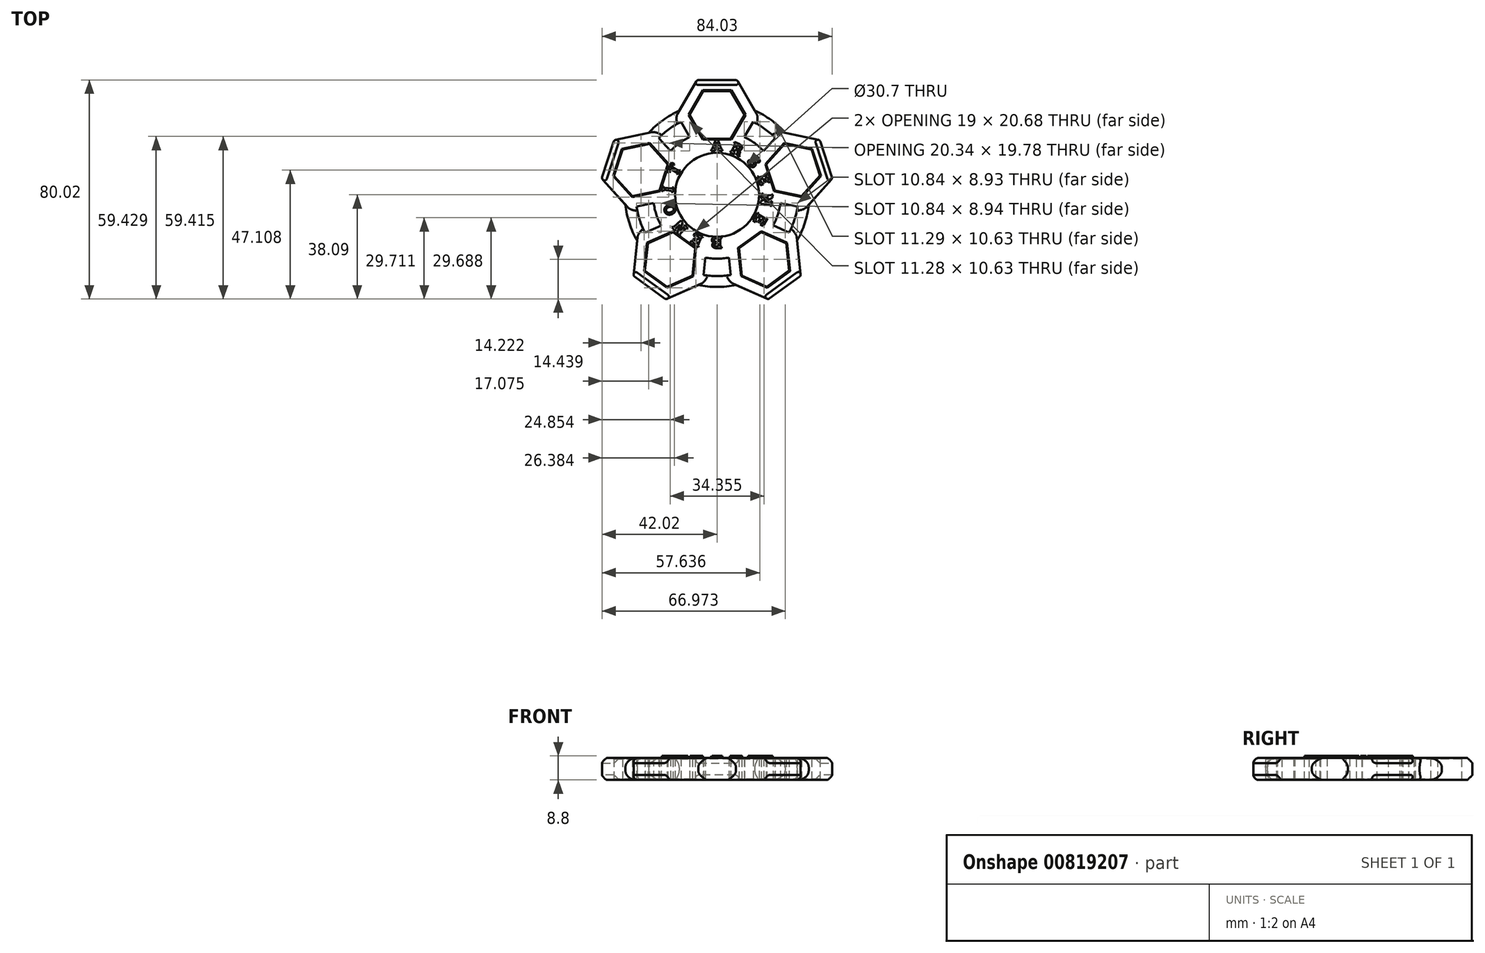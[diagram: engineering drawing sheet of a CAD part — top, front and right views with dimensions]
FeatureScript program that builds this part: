
annotation { "Feature Type Name" : "Feature", "Feature Type Description" : "" }
export const myFeature = defineFeature(function(context is Context, id is Id, definition is map)
    precondition{}
    {
        {
            var Q0;
            Q0=qCreatedBy(makeId("Top.planeOp"),FACE);
            var sketch = newSketch(context, id + "F0", { "sketchPlane" : qUnion([Q0])});
            skCircle(sketch, "E0", {"center": v(0, 0) * mm, "radius": 15.35 * mm});
            skCircle(sketch, "E1", {"center": v(0, 0) * mm, "radius": 23.35 * mm});
            skCircle(sketch, "E2.cCircle", {"center": v(-0.01, 29.22) * mm, "radius": 10.05 * mm, "construction": true});
            skLineSegment(sketch, "E2.0", {"start": v(-5.04, 20.52) * mm, "end": v(-10.06, 29.22) * mm});
            skLineSegment(sketch, "E2.1", {"start": v(-10.06, 29.22) * mm, "end": v(-5.04, 37.93) * mm});
            skLineSegment(sketch, "E2.2", {"start": v(-5.04, 37.93) * mm, "end": v(5.01, 37.93) * mm});
            skLineSegment(sketch, "E2.3", {"start": v(5.01, 37.93) * mm, "end": v(10.04, 29.22) * mm});
            skLineSegment(sketch, "E2.4", {"start": v(10.04, 29.22) * mm, "end": v(5.01, 20.52) * mm});
            skLineSegment(sketch, "E2.5", {"start": v(5.01, 20.52) * mm, "end": v(-5.04, 20.52) * mm});
            skCircle(sketch, "E3", {"center": v(0, 0) * mm, "radius": 29.73 * mm});
            skCircle(sketch, "E4", {"center": v(0, 0) * mm, "radius": 39.45 * mm});
            skLineSegment(sketch, "E5.0", {"start": v(-14.68, 29.22) * mm, "end": v(-7.35, 41.93) * mm});
            skLineSegment(sketch, "E5.1", {"start": v(7.32, 41.93) * mm, "end": v(14.65, 29.22) * mm});
            skLineSegment(sketch, "E5.2", {"start": v(14.65, 29.22) * mm, "end": v(7.32, 16.52) * mm});
            skLineSegment(sketch, "E5.3", {"start": v(-7.35, 41.93) * mm, "end": v(7.32, 41.93) * mm});
            skLineSegment(sketch, "E5.4", {"start": v(7.32, 16.52) * mm, "end": v(-7.35, 16.52) * mm});
            skLineSegment(sketch, "E5.5", {"start": v(-7.35, 16.52) * mm, "end": v(-14.68, 29.22) * mm});
            skCircle(sketch, "E6", {"center": v(0, 0) * mm, "radius": 33.7 * mm});
            skLineSegment(sketch, "E7.1.0", {"start": v(-42.15, 5.97) * mm, "end": v(-37.61, 19.92) * mm});
            skCircle(sketch, "E7.1.1", {"center": v(-27.8, 9.02) * mm, "radius": 10.05 * mm, "construction": true});
            skLineSegment(sketch, "E7.1.2", {"start": v(-37.63, 6.93) * mm, "end": v(-34.52, 16.49) * mm});
            skLineSegment(sketch, "E7.1.3", {"start": v(-34.52, 16.49) * mm, "end": v(-24.7, 18.58) * mm});
            skLineSegment(sketch, "E7.1.4", {"start": v(-30.9, -0.54) * mm, "end": v(-37.63, 6.93) * mm});
            skLineSegment(sketch, "E7.1.5", {"start": v(-21.07, 1.55) * mm, "end": v(-30.9, -0.54) * mm});
            skLineSegment(sketch, "E7.1.6", {"start": v(-17.97, 11.1) * mm, "end": v(-21.07, 1.55) * mm});
            skLineSegment(sketch, "E7.1.7", {"start": v(-24.7, 18.58) * mm, "end": v(-17.97, 11.1) * mm});
            skLineSegment(sketch, "E7.1.8", {"start": v(-37.61, 19.92) * mm, "end": v(-23.27, 22.97) * mm});
            skLineSegment(sketch, "E7.1.9", {"start": v(-17.98, -1.88) * mm, "end": v(-32.33, -4.93) * mm});
            skLineSegment(sketch, "E7.1.10", {"start": v(-13.45, 12.07) * mm, "end": v(-17.98, -1.88) * mm});
            skLineSegment(sketch, "E7.1.11", {"start": v(-23.27, 22.97) * mm, "end": v(-13.45, 12.07) * mm});
            skLineSegment(sketch, "E7.1.12", {"start": v(-32.33, -4.93) * mm, "end": v(-42.15, 5.97) * mm});
            skLineSegment(sketch, "E7.2.0", {"start": v(-18.7, -38.24) * mm, "end": v(-30.57, -29.62) * mm});
            skCircle(sketch, "E7.2.1", {"center": v(-17.17, -23.65) * mm, "radius": 10.05 * mm, "construction": true});
            skLineSegment(sketch, "E7.2.2", {"start": v(-18.22, -33.65) * mm, "end": v(-26.35, -27.74) * mm});
            skLineSegment(sketch, "E7.2.3", {"start": v(-26.35, -27.74) * mm, "end": v(-25.3, -17.74) * mm});
            skLineSegment(sketch, "E7.2.4", {"start": v(-9.04, -29.56) * mm, "end": v(-18.22, -33.65) * mm});
            skLineSegment(sketch, "E7.2.5", {"start": v(-7.99, -19.56) * mm, "end": v(-9.04, -29.56) * mm});
            skLineSegment(sketch, "E7.2.6", {"start": v(-16.12, -13.66) * mm, "end": v(-7.99, -19.56) * mm});
            skLineSegment(sketch, "E7.2.7", {"start": v(-25.3, -17.74) * mm, "end": v(-16.12, -13.66) * mm});
            skLineSegment(sketch, "E7.2.8", {"start": v(-30.57, -29.62) * mm, "end": v(-29.03, -15.03) * mm});
            skLineSegment(sketch, "E7.2.9", {"start": v(-3.77, -17.68) * mm, "end": v(-5.3, -32.27) * mm});
            skLineSegment(sketch, "E7.2.10", {"start": v(-15.63, -9.06) * mm, "end": v(-3.77, -17.68) * mm});
            skLineSegment(sketch, "E7.2.11", {"start": v(-29.03, -15.03) * mm, "end": v(-15.63, -9.06) * mm});
            skLineSegment(sketch, "E7.2.12", {"start": v(-5.3, -32.27) * mm, "end": v(-18.7, -38.24) * mm});
            skLineSegment(sketch, "E7.3.0", {"start": v(30.59, -29.6) * mm, "end": v(18.72, -38.22) * mm});
            skCircle(sketch, "E7.3.1", {"center": v(17.19, -23.63) * mm, "radius": 10.05 * mm, "construction": true});
            skLineSegment(sketch, "E7.3.2", {"start": v(26.37, -27.72) * mm, "end": v(18.24, -33.63) * mm});
            skLineSegment(sketch, "E7.3.3", {"start": v(18.24, -33.63) * mm, "end": v(9.06, -29.54) * mm});
            skLineSegment(sketch, "E7.3.4", {"start": v(25.32, -17.73) * mm, "end": v(26.37, -27.72) * mm});
            skLineSegment(sketch, "E7.3.5", {"start": v(16.14, -13.64) * mm, "end": v(25.32, -17.73) * mm});
            skLineSegment(sketch, "E7.3.6", {"start": v(8, -19.55) * mm, "end": v(16.14, -13.64) * mm});
            skLineSegment(sketch, "E7.3.7", {"start": v(9.06, -29.54) * mm, "end": v(8, -19.55) * mm});
            skLineSegment(sketch, "E7.3.8", {"start": v(18.72, -38.22) * mm, "end": v(5.32, -32.26) * mm});
            skLineSegment(sketch, "E7.3.9", {"start": v(15.66, -9.05) * mm, "end": v(29.06, -15.01) * mm});
            skLineSegment(sketch, "E7.3.10", {"start": v(3.79, -17.67) * mm, "end": v(15.66, -9.05) * mm});
            skLineSegment(sketch, "E7.3.11", {"start": v(5.32, -32.26) * mm, "end": v(3.79, -17.67) * mm});
            skLineSegment(sketch, "E7.3.12", {"start": v(29.06, -15.01) * mm, "end": v(30.59, -29.6) * mm});
            skLineSegment(sketch, "E7.4.0", {"start": v(37.6, 19.95) * mm, "end": v(42.14, 6) * mm});
            skCircle(sketch, "E7.4.1", {"center": v(27.79, 9.04) * mm, "radius": 10.05 * mm, "construction": true});
            skLineSegment(sketch, "E7.4.2", {"start": v(34.51, 16.51) * mm, "end": v(37.62, 6.95) * mm});
            skLineSegment(sketch, "E7.4.3", {"start": v(37.62, 6.95) * mm, "end": v(30.9, -0.51) * mm});
            skLineSegment(sketch, "E7.4.4", {"start": v(24.68, 18.6) * mm, "end": v(34.51, 16.51) * mm});
            skLineSegment(sketch, "E7.4.5", {"start": v(17.96, 11.13) * mm, "end": v(24.68, 18.6) * mm});
            skLineSegment(sketch, "E7.4.6", {"start": v(21.06, 1.58) * mm, "end": v(17.96, 11.13) * mm});
            skLineSegment(sketch, "E7.4.7", {"start": v(30.9, -0.51) * mm, "end": v(21.06, 1.58) * mm});
            skLineSegment(sketch, "E7.4.8", {"start": v(42.14, 6) * mm, "end": v(32.32, -4.9) * mm});
            skLineSegment(sketch, "E7.4.9", {"start": v(13.44, 12.1) * mm, "end": v(23.26, 23) * mm});
            skLineSegment(sketch, "E7.4.10", {"start": v(17.97, -1.86) * mm, "end": v(13.44, 12.1) * mm});
            skLineSegment(sketch, "E7.4.11", {"start": v(32.32, -4.9) * mm, "end": v(17.97, -1.86) * mm});
            skLineSegment(sketch, "E7.4.12", {"start": v(23.26, 23) * mm, "end": v(37.6, 19.95) * mm});
            skSolve(sketch);
        }
        {
            var Q0;
            {var subQ1=sQuery(id+"F0.wireOp",EDGE,"E2.0");var subQ5=sQuery(id+"F0.wireOp",EDGE,"E2.1");var subQ6=makeQuery(id+"F0.imprint","INTERSECT",VERTEX,{"derivedFrom":[subQ1,subQ5]});Q0=makeQuery(id+"F0.imprint","IMPRINT",FACE,{"disambiguationData":[TD([[makeQuery(id+"F0.imprint","IMPRINT",EDGE,{"disambiguationData":[TD([[subQ6,1.0]])],"derivedFrom":subQ1}),1.0]])]});}
            var Q1;
            {var subQ1=sQuery(id+"F0.wireOp",EDGE,"E2.4");var subQ9=sQuery(id+"F0.wireOp",EDGE,"E2.3");var subQ10=makeQuery(id+"F0.imprint","INTERSECT",VERTEX,{"derivedFrom":[subQ9,subQ1]});Q1=makeQuery(id+"F0.imprint","IMPRINT",FACE,{"disambiguationData":[TD([[makeQuery(id+"F0.imprint","IMPRINT",EDGE,{"disambiguationData":[TD([[subQ10,1.0]])],"derivedFrom":subQ9}),1.0]])]});}
            var Q2;
            {var subQ5=sQuery(id+"F0.wireOp",EDGE,"E3");var subQ9=sQuery(id+"F0.wireOp",EDGE,"E7.4.9");var subQ10=makeQuery(id+"F0.imprint","INTERSECT",VERTEX,{"derivedFrom":[subQ5,subQ9]});Q2=makeQuery(id+"F0.imprint","IMPRINT",FACE,{"disambiguationData":[TD([[makeQuery(id+"F0.imprint","IMPRINT",EDGE,{"disambiguationData":[TD([[subQ10,1.0]])],"derivedFrom":subQ5}),-1.0]])]});}
            var Q3;
            {var subQ7=sQuery(id+"F0.wireOp",EDGE,"E3");var subQ9=sQuery(id+"F0.wireOp",EDGE,"E7.4.9");var subQ10=makeQuery(id+"F0.imprint","INTERSECT",VERTEX,{"derivedFrom":[subQ7,subQ9]});Q3=makeQuery(id+"F0.imprint","IMPRINT",FACE,{"disambiguationData":[TD([[makeQuery(id+"F0.imprint","IMPRINT",EDGE,{"disambiguationData":[TD([[subQ10,-1.0]])],"derivedFrom":subQ7}),-1.0]])]});}
            var Q4;
            {var subQ0=sQuery(id+"F0.wireOp",EDGE,"E5.5");var subQ3=sQuery(id+"F0.wireOp",EDGE,"E3");var subQ4=makeQuery(id+"F0.imprint","INTERSECT",VERTEX,{"derivedFrom":[subQ3,subQ0]});Q4=makeQuery(id+"F0.imprint","IMPRINT",FACE,{"disambiguationData":[TD([[makeQuery(id+"F0.imprint","IMPRINT",EDGE,{"disambiguationData":[TD([[subQ4,-1.0]])],"derivedFrom":subQ3}),-1.0]])]});}
            var Q5;
            {var subQ3=sQuery(id+"F0.wireOp",EDGE,"E3");var subQ9=sQuery(id+"F0.wireOp",EDGE,"E7.1.11");var subQ11=makeQuery(id+"F0.imprint","INTERSECT",VERTEX,{"derivedFrom":[subQ3,subQ9]});Q5=makeQuery(id+"F0.imprint","IMPRINT",FACE,{"disambiguationData":[TD([[makeQuery(id+"F0.imprint","IMPRINT",EDGE,{"disambiguationData":[TD([[subQ11,-1.0]])],"derivedFrom":subQ3}),-1.0]])]});}
            var Q6;
            {var subQ0=sQuery(id+"F0.wireOp",EDGE,"E7.1.5");var subQ3=sQuery(id+"F0.wireOp",EDGE,"E3");var subQ4=makeQuery(id+"F0.imprint","INTERSECT",VERTEX,{"derivedFrom":[subQ3,subQ0]});Q6=makeQuery(id+"F0.imprint","IMPRINT",FACE,{"disambiguationData":[TD([[makeQuery(id+"F0.imprint","IMPRINT",EDGE,{"disambiguationData":[TD([[subQ4,-1.0]])],"derivedFrom":subQ3}),-1.0]])]});}
            var Q7;
            {var subQ1=sQuery(id+"F0.wireOp",EDGE,"E7.1.9");var subQ7=sQuery(id+"F0.wireOp",EDGE,"E3");var subQ8=makeQuery(id+"F0.imprint","INTERSECT",VERTEX,{"derivedFrom":[subQ7,subQ1]});Q7=makeQuery(id+"F0.imprint","IMPRINT",FACE,{"disambiguationData":[TD([[makeQuery(id+"F0.imprint","IMPRINT",EDGE,{"disambiguationData":[TD([[subQ8,-1.0]])],"derivedFrom":subQ7}),-1.0]])]});}
            var Q8;
            {var subQ5=sQuery(id+"F0.wireOp",EDGE,"E3");var subQ9=sQuery(id+"F0.wireOp",EDGE,"E7.2.11");var subQ11=makeQuery(id+"F0.imprint","INTERSECT",VERTEX,{"derivedFrom":[subQ5,subQ9]});Q8=makeQuery(id+"F0.imprint","IMPRINT",FACE,{"disambiguationData":[TD([[makeQuery(id+"F0.imprint","IMPRINT",EDGE,{"disambiguationData":[TD([[subQ11,-1.0]])],"derivedFrom":subQ5}),-1.0]])]});}
            var Q9;
            {var subQ0=sQuery(id+"F0.wireOp",EDGE,"E7.2.5");var subQ3=sQuery(id+"F0.wireOp",EDGE,"E3");var subQ4=makeQuery(id+"F0.imprint","INTERSECT",VERTEX,{"derivedFrom":[subQ3,subQ0]});Q9=makeQuery(id+"F0.imprint","IMPRINT",FACE,{"disambiguationData":[TD([[makeQuery(id+"F0.imprint","IMPRINT",EDGE,{"disambiguationData":[TD([[subQ4,-1.0]])],"derivedFrom":subQ3}),-1.0]])]});}
            var Q10;
            {var subQ1=sQuery(id+"F0.wireOp",EDGE,"E7.2.9");var subQ7=sQuery(id+"F0.wireOp",EDGE,"E3");var subQ8=makeQuery(id+"F0.imprint","INTERSECT",VERTEX,{"derivedFrom":[subQ7,subQ1]});Q10=makeQuery(id+"F0.imprint","IMPRINT",FACE,{"disambiguationData":[TD([[makeQuery(id+"F0.imprint","IMPRINT",EDGE,{"disambiguationData":[TD([[subQ8,-1.0]])],"derivedFrom":subQ7}),-1.0]])]});}
            var Q11;
            {var subQ3=sQuery(id+"F0.wireOp",EDGE,"E3");var subQ9=sQuery(id+"F0.wireOp",EDGE,"E7.3.11");var subQ11=makeQuery(id+"F0.imprint","INTERSECT",VERTEX,{"derivedFrom":[subQ3,subQ9]});Q11=makeQuery(id+"F0.imprint","IMPRINT",FACE,{"disambiguationData":[TD([[makeQuery(id+"F0.imprint","IMPRINT",EDGE,{"disambiguationData":[TD([[subQ11,-1.0]])],"derivedFrom":subQ3}),-1.0]])]});}
            var Q12;
            {var subQ0=sQuery(id+"F0.wireOp",EDGE,"E7.3.5");var subQ3=sQuery(id+"F0.wireOp",EDGE,"E3");var subQ4=makeQuery(id+"F0.imprint","INTERSECT",VERTEX,{"derivedFrom":[subQ3,subQ0]});Q12=makeQuery(id+"F0.imprint","IMPRINT",FACE,{"disambiguationData":[TD([[makeQuery(id+"F0.imprint","IMPRINT",EDGE,{"disambiguationData":[TD([[subQ4,-1.0]])],"derivedFrom":subQ3}),-1.0]])]});}
            var Q13;
            {var subQ1=sQuery(id+"F0.wireOp",EDGE,"E7.3.9");var subQ7=sQuery(id+"F0.wireOp",EDGE,"E3");var subQ8=makeQuery(id+"F0.imprint","INTERSECT",VERTEX,{"derivedFrom":[subQ7,subQ1]});Q13=makeQuery(id+"F0.imprint","IMPRINT",FACE,{"disambiguationData":[TD([[makeQuery(id+"F0.imprint","IMPRINT",EDGE,{"disambiguationData":[TD([[subQ8,-1.0]])],"derivedFrom":subQ7}),-1.0]])]});}
            var Q14;
            {var subQ3=sQuery(id+"F0.wireOp",EDGE,"E3");var subQ9=sQuery(id+"F0.wireOp",EDGE,"E7.4.11");var subQ11=makeQuery(id+"F0.imprint","INTERSECT",VERTEX,{"derivedFrom":[subQ3,subQ9]});Q14=makeQuery(id+"F0.imprint","IMPRINT",FACE,{"disambiguationData":[TD([[makeQuery(id+"F0.imprint","IMPRINT",EDGE,{"disambiguationData":[TD([[subQ11,-1.0]])],"derivedFrom":subQ3}),-1.0]])]});}
            var Q15;
            {var subQ5=sQuery(id+"F0.wireOp",EDGE,"E5.3");Q15=makeQuery(id+"F0.imprint","IMPRINT",FACE,{"disambiguationData":[TD([[makeQuery(id+"F0.imprint","IMPRINT",EDGE,{"derivedFrom":subQ5}),-1.0]])]});}
            var Q16;
            {var subQ1=sQuery(id+"F0.wireOp",EDGE,"E2.2");Q16=makeQuery(id+"F0.imprint","IMPRINT",FACE,{"disambiguationData":[TD([[makeQuery(id+"F0.imprint","IMPRINT",EDGE,{"derivedFrom":subQ1}),1.0]])]});}
            var Q17;
            {var subQ0=sQuery(id+"F0.wireOp",EDGE,"E7.4.2");Q17=makeQuery(id+"F0.imprint","IMPRINT",FACE,{"disambiguationData":[TD([[makeQuery(id+"F0.imprint","IMPRINT",EDGE,{"derivedFrom":subQ0}),1.0]])]});}
            var Q18;
            {var subQ0=sQuery(id+"F0.wireOp",EDGE,"E7.1.2");Q18=makeQuery(id+"F0.imprint","IMPRINT",FACE,{"disambiguationData":[TD([[makeQuery(id+"F0.imprint","IMPRINT",EDGE,{"derivedFrom":subQ0}),1.0]])]});}
            var Q19;
            {var subQ9=sQuery(id+"F0.wireOp",EDGE,"E7.2.2");Q19=makeQuery(id+"F0.imprint","IMPRINT",FACE,{"disambiguationData":[TD([[makeQuery(id+"F0.imprint","IMPRINT",EDGE,{"derivedFrom":subQ9}),1.0]])]});}
            var Q20;
            {var subQ0=sQuery(id+"F0.wireOp",EDGE,"E7.3.2");Q20=makeQuery(id+"F0.imprint","IMPRINT",FACE,{"disambiguationData":[TD([[makeQuery(id+"F0.imprint","IMPRINT",EDGE,{"derivedFrom":subQ0}),1.0]])]});}
            var Q21;
            {var subQ0=sQuery(id+"F0.wireOp",EDGE,"E5.2");var subQ1=sQuery(id+"F0.wireOp",EDGE,"E1");var subQ2=makeQuery(id+"F0.imprint","INTERSECT",VERTEX,{"derivedFrom":[subQ1,subQ0]});Q21=makeQuery(id+"F0.imprint","IMPRINT",FACE,{"disambiguationData":[TD([[makeQuery(id+"F0.imprint","IMPRINT",EDGE,{"disambiguationData":[TD([[subQ2,-1.0]])],"derivedFrom":subQ1}),-1.0]])]});}
            var Q22;
            {var subQ0=sQuery(id+"F0.wireOp",EDGE,"E2.0");var subQ1=sQuery(id+"F0.wireOp",EDGE,"E1");var subQ2=makeQuery(id+"F0.imprint","INTERSECT",VERTEX,{"derivedFrom":[subQ1,subQ0]});Q22=makeQuery(id+"F0.imprint","IMPRINT",FACE,{"disambiguationData":[TD([[makeQuery(id+"F0.imprint","IMPRINT",EDGE,{"disambiguationData":[TD([[subQ2,-1.0]])],"derivedFrom":subQ1}),-1.0]])]});}
            var Q23;
            {var subQ0=sQuery(id+"F0.wireOp",EDGE,"E2.5");Q23=makeQuery(id+"F0.imprint","IMPRINT",FACE,{"disambiguationData":[TD([[makeQuery(id+"F0.imprint","IMPRINT",EDGE,{"derivedFrom":subQ0}),1.0]])]});}
            var Q24;
            {var subQ5=sQuery(id+"F0.wireOp",EDGE,"E7.1.0");Q24=makeQuery(id+"F0.imprint","IMPRINT",FACE,{"disambiguationData":[TD([[makeQuery(id+"F0.imprint","IMPRINT",EDGE,{"derivedFrom":subQ5}),-1.0]])]});}
            var Q25;
            {var subQ0=sQuery(id+"F0.wireOp",EDGE,"E7.4.5");var subQ1=sQuery(id+"F0.wireOp",EDGE,"E1");var subQ2=makeQuery(id+"F0.imprint","INTERSECT",VERTEX,{"derivedFrom":[subQ1,subQ0]});Q25=makeQuery(id+"F0.imprint","IMPRINT",FACE,{"disambiguationData":[TD([[makeQuery(id+"F0.imprint","IMPRINT",EDGE,{"disambiguationData":[TD([[subQ2,-1.0]])],"derivedFrom":subQ1}),-1.0]])]});}
            var Q26;
            {var subQ0=sQuery(id+"F0.wireOp",EDGE,"E7.4.6");Q26=makeQuery(id+"F0.imprint","IMPRINT",FACE,{"disambiguationData":[TD([[makeQuery(id+"F0.imprint","IMPRINT",EDGE,{"derivedFrom":subQ0}),1.0]])]});}
            var Q27;
            Q27=makeQuery(id+"F0.imprint","IMPRINT",FACE,{"disambiguationData":[TD([[makeQuery(id+"F0.imprint","IMPRINT",EDGE,{"derivedFrom":sQuery(id+"F0.wireOp",EDGE,"E0")}),-1.0]])]});
            var Q28;
            {var subQ5=sQuery(id+"F0.wireOp",EDGE,"E7.4.0");Q28=makeQuery(id+"F0.imprint","IMPRINT",FACE,{"disambiguationData":[TD([[makeQuery(id+"F0.imprint","IMPRINT",EDGE,{"derivedFrom":subQ5}),-1.0]])]});}
            var Q29;
            {var subQ0=sQuery(id+"F0.wireOp",EDGE,"E7.1.6");Q29=makeQuery(id+"F0.imprint","IMPRINT",FACE,{"disambiguationData":[TD([[makeQuery(id+"F0.imprint","IMPRINT",EDGE,{"derivedFrom":subQ0}),1.0]])]});}
            var Q30;
            {var subQ0=sQuery(id+"F0.wireOp",EDGE,"E7.2.6");Q30=makeQuery(id+"F0.imprint","IMPRINT",FACE,{"disambiguationData":[TD([[makeQuery(id+"F0.imprint","IMPRINT",EDGE,{"derivedFrom":subQ0}),1.0]])]});}
            var Q31;
            {var subQ0=sQuery(id+"F0.wireOp",EDGE,"E7.3.6");Q31=makeQuery(id+"F0.imprint","IMPRINT",FACE,{"disambiguationData":[TD([[makeQuery(id+"F0.imprint","IMPRINT",EDGE,{"derivedFrom":subQ0}),1.0]])]});}
            var Q32;
            {var subQ0=sQuery(id+"F0.wireOp",EDGE,"E7.3.5");var subQ1=sQuery(id+"F0.wireOp",EDGE,"E1");var subQ2=makeQuery(id+"F0.imprint","INTERSECT",VERTEX,{"derivedFrom":[subQ1,subQ0]});Q32=makeQuery(id+"F0.imprint","IMPRINT",FACE,{"disambiguationData":[TD([[makeQuery(id+"F0.imprint","IMPRINT",EDGE,{"disambiguationData":[TD([[subQ2,-1.0]])],"derivedFrom":subQ1}),-1.0]])]});}
            var Q33;
            {var subQ0=sQuery(id+"F0.wireOp",EDGE,"E7.3.11");var subQ1=sQuery(id+"F0.wireOp",EDGE,"E1");var subQ2=makeQuery(id+"F0.imprint","INTERSECT",VERTEX,{"derivedFrom":[subQ1,subQ0]});Q33=makeQuery(id+"F0.imprint","IMPRINT",FACE,{"disambiguationData":[TD([[makeQuery(id+"F0.imprint","IMPRINT",EDGE,{"disambiguationData":[TD([[subQ2,-1.0]])],"derivedFrom":subQ1}),-1.0]])]});}
            var Q34;
            {var subQ0=sQuery(id+"F0.wireOp",EDGE,"E7.2.5");var subQ1=sQuery(id+"F0.wireOp",EDGE,"E1");var subQ2=makeQuery(id+"F0.imprint","INTERSECT",VERTEX,{"derivedFrom":[subQ1,subQ0]});Q34=makeQuery(id+"F0.imprint","IMPRINT",FACE,{"disambiguationData":[TD([[makeQuery(id+"F0.imprint","IMPRINT",EDGE,{"disambiguationData":[TD([[subQ2,-1.0]])],"derivedFrom":subQ1}),-1.0]])]});}
            var Q35;
            {var subQ0=sQuery(id+"F0.wireOp",EDGE,"E7.2.11");var subQ1=sQuery(id+"F0.wireOp",EDGE,"E1");var subQ2=makeQuery(id+"F0.imprint","INTERSECT",VERTEX,{"derivedFrom":[subQ1,subQ0]});Q35=makeQuery(id+"F0.imprint","IMPRINT",FACE,{"disambiguationData":[TD([[makeQuery(id+"F0.imprint","IMPRINT",EDGE,{"disambiguationData":[TD([[subQ2,-1.0]])],"derivedFrom":subQ1}),-1.0]])]});}
            var Q36;
            {var subQ0=sQuery(id+"F0.wireOp",EDGE,"E7.1.5");var subQ1=sQuery(id+"F0.wireOp",EDGE,"E1");var subQ2=makeQuery(id+"F0.imprint","INTERSECT",VERTEX,{"derivedFrom":[subQ1,subQ0]});Q36=makeQuery(id+"F0.imprint","IMPRINT",FACE,{"disambiguationData":[TD([[makeQuery(id+"F0.imprint","IMPRINT",EDGE,{"disambiguationData":[TD([[subQ2,-1.0]])],"derivedFrom":subQ1}),-1.0]])]});}
            var Q37;
            {var subQ0=sQuery(id+"F0.wireOp",EDGE,"E7.1.11");var subQ1=sQuery(id+"F0.wireOp",EDGE,"E1");var subQ2=makeQuery(id+"F0.imprint","INTERSECT",VERTEX,{"derivedFrom":[subQ1,subQ0]});Q37=makeQuery(id+"F0.imprint","IMPRINT",FACE,{"disambiguationData":[TD([[makeQuery(id+"F0.imprint","IMPRINT",EDGE,{"disambiguationData":[TD([[subQ2,-1.0]])],"derivedFrom":subQ1}),-1.0]])]});}
            var Q38;
            {var subQ5=sQuery(id+"F0.wireOp",EDGE,"E7.2.0");Q38=makeQuery(id+"F0.imprint","IMPRINT",FACE,{"disambiguationData":[TD([[makeQuery(id+"F0.imprint","IMPRINT",EDGE,{"derivedFrom":subQ5}),-1.0]])]});}
            var Q39;
            {var subQ5=sQuery(id+"F0.wireOp",EDGE,"E7.3.0");Q39=makeQuery(id+"F0.imprint","IMPRINT",FACE,{"disambiguationData":[TD([[makeQuery(id+"F0.imprint","IMPRINT",EDGE,{"derivedFrom":subQ5}),-1.0]])]});}
            var Q40;
            {var subQ0=sQuery(id+"F0.wireOp",EDGE,"E7.4.7");var subQ1=sQuery(id+"F0.wireOp",EDGE,"E1");var subQ2=makeQuery(id+"F0.imprint","INTERSECT",VERTEX,{"derivedFrom":[subQ1,subQ0]});Q40=makeQuery(id+"F0.imprint","IMPRINT",FACE,{"disambiguationData":[TD([[makeQuery(id+"F0.imprint","IMPRINT",EDGE,{"disambiguationData":[TD([[subQ2,1.0]])],"derivedFrom":subQ1}),-1.0]])]});}
            extrude(context, id + "F1", {"entities" : qUnion([Q0, Q1, Q2, Q3, Q4, Q5, Q6, Q7, Q8, Q9, Q10, Q11, Q12, Q13, Q14, Q15, Q16, Q17, Q18, Q19, Q20, Q21, Q22, Q23, Q24, Q25, Q26, Q27, Q28, Q29, Q30, Q31, Q32, Q33, Q34, Q35, Q36, Q37, Q38, Q39, Q40]), "endBound" : BoundingType.SYMMETRIC, "depth" : 8 * mm, "offsetDistance" : 25 * mm});
        }
        {
            var Q0;
            {var subQ0=sQuery(id+"F0.wireOp",EDGE,"E4");Q0=makeQuery(id+"F1.opExtrude","CAP_EDGE",EDGE,{"disambiguationData":[OSD([subQ0]),TDD([makeQuery(id+"F0.imprint","IMPRINT",EDGE,{"disambiguationData":[TD([[makeQuery(id+"F0.imprint","INTERSECT",VERTEX,{"derivedFrom":[subQ0,sQuery(id+"F0.wireOp",EDGE,"E5.0")]}),-1.0]])],"derivedFrom":subQ0})])],"isStart":false});}
            var Q1;
            {var subQ0=sQuery(id+"F0.wireOp",EDGE,"E4");Q1=makeQuery(id+"F1.opExtrude","CAP_EDGE",EDGE,{"disambiguationData":[OSD([subQ0]),TDD([makeQuery(id+"F0.imprint","IMPRINT",EDGE,{"disambiguationData":[TD([[makeQuery(id+"F0.imprint","INTERSECT",VERTEX,{"derivedFrom":[subQ0,sQuery(id+"F0.wireOp",EDGE,"E5.2")]}),1.0]])],"derivedFrom":subQ0})])],"isStart":false});}
            var Q2;
            {var subQ0=sQuery(id+"F0.wireOp",EDGE,"E4");Q2=makeQuery(id+"F1.opExtrude","CAP_EDGE",EDGE,{"disambiguationData":[OSD([subQ0]),TDD([makeQuery(id+"F0.imprint","IMPRINT",EDGE,{"disambiguationData":[TD([[makeQuery(id+"F0.imprint","INTERSECT",VERTEX,{"derivedFrom":[subQ0,sQuery(id+"F0.wireOp",EDGE,"16fe0f86-ba45-4510-805f-83fab8150242.4")]}),-1.0]])],"derivedFrom":subQ0})])],"isStart":false});}
            var Q3;
            {var subQ0=sQuery(id+"F0.wireOp",EDGE,"E4");Q3=makeQuery(id+"F1.opExtrude","CAP_EDGE",EDGE,{"disambiguationData":[OSD([subQ0]),TDD([makeQuery(id+"F0.imprint","IMPRINT",EDGE,{"disambiguationData":[TD([[makeQuery(id+"F0.imprint","INTERSECT",VERTEX,{"derivedFrom":[subQ0,sQuery(id+"F0.wireOp",EDGE,"16fe0f86-ba45-4510-805f-83fab8150242.4")]}),-1.0]])],"derivedFrom":subQ0})])],"isStart":true});}
            var Q4;
            {var subQ0=sQuery(id+"F0.wireOp",EDGE,"E4");Q4=makeQuery(id+"F1.opExtrude","CAP_EDGE",EDGE,{"disambiguationData":[OSD([subQ0]),TDD([makeQuery(id+"F0.imprint","IMPRINT",EDGE,{"disambiguationData":[TD([[makeQuery(id+"F0.imprint","INTERSECT",VERTEX,{"derivedFrom":[subQ0,sQuery(id+"F0.wireOp",EDGE,"E5.0")]}),-1.0]])],"derivedFrom":subQ0})])],"isStart":true});}
            var Q5;
            {var subQ0=sQuery(id+"F0.wireOp",EDGE,"E6");Q5=makeQuery(id+"F1.opExtrude","CAP_EDGE",EDGE,{"disambiguationData":[OSD([subQ0]),TDD([makeQuery(id+"F0.imprint","IMPRINT",EDGE,{"disambiguationData":[TD([[makeQuery(id+"F0.imprint","INTERSECT",VERTEX,{"derivedFrom":[sQuery(id+"F0.wireOp",EDGE,"7660e7ec-dfda-4ca4-bfb6-eb722cb9b26f.2.2"),subQ0]}),1.0]])],"derivedFrom":subQ0})])],"isStart":true});}
            var Q6;
            {var subQ0=sQuery(id+"F0.wireOp",EDGE,"E6");Q6=makeQuery(id+"F1.opExtrude","CAP_EDGE",EDGE,{"disambiguationData":[OSD([subQ0]),TDD([makeQuery(id+"F0.imprint","IMPRINT",EDGE,{"disambiguationData":[TD([[makeQuery(id+"F0.imprint","INTERSECT",VERTEX,{"derivedFrom":[sQuery(id+"F0.wireOp",EDGE,"7660e7ec-dfda-4ca4-bfb6-eb722cb9b26f.2.2"),subQ0]}),1.0]])],"derivedFrom":subQ0})])],"isStart":false});}
            var Q7;
            {var subQ0=sQuery(id+"F0.wireOp",EDGE,"E6");Q7=makeQuery(id+"F1.opExtrude","CAP_EDGE",EDGE,{"disambiguationData":[OSD([subQ0]),TDD([makeQuery(id+"F0.imprint","IMPRINT",EDGE,{"disambiguationData":[TD([[makeQuery(id+"F0.imprint","INTERSECT",VERTEX,{"derivedFrom":[sQuery(id+"F0.wireOp",EDGE,"16fe0f86-ba45-4510-805f-83fab8150242.3"),subQ0]}),1.0]])],"derivedFrom":subQ0})])],"isStart":true});}
            var Q8;
            {var subQ0=sQuery(id+"F0.wireOp",EDGE,"E6");Q8=makeQuery(id+"F1.opExtrude","CAP_EDGE",EDGE,{"disambiguationData":[OSD([subQ0]),TDD([makeQuery(id+"F0.imprint","IMPRINT",EDGE,{"disambiguationData":[TD([[makeQuery(id+"F0.imprint","INTERSECT",VERTEX,{"derivedFrom":[sQuery(id+"F0.wireOp",EDGE,"16fe0f86-ba45-4510-805f-83fab8150242.3"),subQ0]}),1.0]])],"derivedFrom":subQ0})])],"isStart":false});}
            var Q9;
            {var subQ0=sQuery(id+"F0.wireOp",EDGE,"E6");Q9=makeQuery(id+"F1.opExtrude","CAP_EDGE",EDGE,{"disambiguationData":[OSD([subQ0]),TDD([makeQuery(id+"F0.imprint","IMPRINT",EDGE,{"disambiguationData":[TD([[makeQuery(id+"F0.imprint","INTERSECT",VERTEX,{"derivedFrom":[sQuery(id+"F0.wireOp",EDGE,"7660e7ec-dfda-4ca4-bfb6-eb722cb9b26f.4.5"),subQ0]}),-1.0]])],"derivedFrom":subQ0})])],"isStart":false});}
            var Q10;
            {var subQ0=sQuery(id+"F0.wireOp",EDGE,"E6");Q10=makeQuery(id+"F1.opExtrude","CAP_EDGE",EDGE,{"disambiguationData":[OSD([subQ0]),TDD([makeQuery(id+"F0.imprint","IMPRINT",EDGE,{"disambiguationData":[TD([[makeQuery(id+"F0.imprint","INTERSECT",VERTEX,{"derivedFrom":[sQuery(id+"F0.wireOp",EDGE,"7660e7ec-dfda-4ca4-bfb6-eb722cb9b26f.4.5"),subQ0]}),-1.0]])],"derivedFrom":subQ0})])],"isStart":true});}
            var Q11;
            {var subQ0=sQuery(id+"F0.wireOp",EDGE,"E4");Q11=makeQuery(id+"F1.opExtrude","CAP_EDGE",EDGE,{"disambiguationData":[OSD([subQ0]),TDD([makeQuery(id+"F0.imprint","IMPRINT",EDGE,{"disambiguationData":[TD([[makeQuery(id+"F0.imprint","INTERSECT",VERTEX,{"derivedFrom":[subQ0,sQuery(id+"F0.wireOp",EDGE,"E5.2")]}),1.0]])],"derivedFrom":subQ0})])],"isStart":true});}
            fillet(context, id + "F2", {"entities" : qUnion([Q0, Q1, Q2, Q3, Q4, Q5, Q6, Q7, Q8, Q9, Q10, Q11]), "radius" : 3.5 * mm, "tangentPropagation" : true, "allowEdgeOverflow" : false});
        }
        {
            var Q0;
            Q0=makeQuery(id+"F0.imprint","IMPRINT",FACE,{"disambiguationData":[TD([[makeQuery(id+"F0.imprint","IMPRINT",EDGE,{"derivedFrom":sQuery(id+"F0.wireOp",EDGE,"E0")}),-1.0]])]});
            extrude(context, id + "F3", {"entities" : qUnion([Q0]), "operationType" : NewBodyOperationType.ADD, "endBound" : BoundingType.SYMMETRIC, "depth" : 7 * mm, "offsetDistance" : 25 * mm});
        }
        {
            var Q0;
            Q0=makeQuery(id+"F1.opExtrude","CAP_EDGE",EDGE,{"disambiguationData":[OSD([sQuery(id+"F0.wireOp",EDGE,"E7.1.0")])],"isStart":true});
            var Q1;
            Q1=makeQuery(id+"F1.opExtrude","CAP_EDGE",EDGE,{"disambiguationData":[OSD([sQuery(id+"F0.wireOp",EDGE,"E7.1.0")])],"isStart":false});
            var Q2;
            Q2=makeQuery(id+"F1.opExtrude","CAP_EDGE",EDGE,{"disambiguationData":[OSD([sQuery(id+"F0.wireOp",EDGE,"E7.3.0")])],"isStart":true});
            var Q3;
            Q3=makeQuery(id+"F1.opExtrude","CAP_EDGE",EDGE,{"disambiguationData":[OSD([sQuery(id+"F0.wireOp",EDGE,"E7.2.0")])],"isStart":true});
            var Q4;
            Q4=makeQuery(id+"F1.opExtrude","CAP_EDGE",EDGE,{"disambiguationData":[OSD([sQuery(id+"F0.wireOp",EDGE,"E7.2.0")])],"isStart":false});
            var Q5;
            Q5=makeQuery(id+"F1.opExtrude","CAP_EDGE",EDGE,{"disambiguationData":[OSD([sQuery(id+"F0.wireOp",EDGE,"E7.3.0")])],"isStart":false});
            var Q6;
            Q6=makeQuery(id+"F1.opExtrude","CAP_EDGE",EDGE,{"disambiguationData":[OSD([sQuery(id+"F0.wireOp",EDGE,"E7.4.0")])],"isStart":false});
            var Q7;
            Q7=makeQuery(id+"F1.opExtrude","CAP_EDGE",EDGE,{"disambiguationData":[OSD([sQuery(id+"F0.wireOp",EDGE,"E5.3")])],"isStart":false});
            var Q8;
            Q8=makeQuery(id+"F1.opExtrude","CAP_EDGE",EDGE,{"disambiguationData":[OSD([sQuery(id+"F0.wireOp",EDGE,"E7.4.0")])],"isStart":true});
            var Q9;
            Q9=makeQuery(id+"F1.opExtrude","CAP_EDGE",EDGE,{"disambiguationData":[OSD([sQuery(id+"F0.wireOp",EDGE,"E5.3")])],"isStart":true});
            chamfer(context, id + "F4", {"entities" : qUnion([Q0, Q1, Q2, Q3, Q4, Q5, Q6, Q7, Q8, Q9]), "width" : 1.8 * mm, "tangentPropagation" : true});
        }
        {
            var Q0;
            Q0=makeQuery(id+"F1.opExtrude","CAP_EDGE",EDGE,{"disambiguationData":[OSD([sQuery(id+"F0.wireOp",EDGE,"E7.3.8")])],"isStart":true});
            var Q1;
            Q1=makeQuery(id+"F1.opExtrude","CAP_EDGE",EDGE,{"disambiguationData":[OSD([sQuery(id+"F0.wireOp",EDGE,"E7.3.8")])],"isStart":false});
            var Q2;
            Q2=makeQuery(id+"F1.opExtrude","CAP_EDGE",EDGE,{"disambiguationData":[OSD([sQuery(id+"F0.wireOp",EDGE,"E7.3.12")])],"isStart":true});
            var Q3;
            Q3=makeQuery(id+"F1.opExtrude","CAP_EDGE",EDGE,{"disambiguationData":[OSD([sQuery(id+"F0.wireOp",EDGE,"E7.3.12")])],"isStart":false});
            var Q4;
            Q4=makeQuery(id+"F1.opExtrude","CAP_EDGE",EDGE,{"disambiguationData":[OSD([sQuery(id+"F0.wireOp",EDGE,"E5.1")])],"isStart":true});
            var Q5;
            Q5=makeQuery(id+"F1.opExtrude","CAP_EDGE",EDGE,{"disambiguationData":[OSD([sQuery(id+"F0.wireOp",EDGE,"E5.0")])],"isStart":true});
            var Q6;
            Q6=makeQuery(id+"F1.opExtrude","CAP_EDGE",EDGE,{"disambiguationData":[OSD([sQuery(id+"F0.wireOp",EDGE,"E7.2.8")])],"isStart":true});
            var Q7;
            Q7=makeQuery(id+"F1.opExtrude","CAP_EDGE",EDGE,{"disambiguationData":[OSD([sQuery(id+"F0.wireOp",EDGE,"E7.2.12")])],"isStart":true});
            var Q8;
            Q8=makeQuery(id+"F1.opExtrude","CAP_EDGE",EDGE,{"disambiguationData":[OSD([sQuery(id+"F0.wireOp",EDGE,"E7.2.12")])],"isStart":false});
            var Q9;
            Q9=makeQuery(id+"F1.opExtrude","CAP_EDGE",EDGE,{"disambiguationData":[OSD([sQuery(id+"F0.wireOp",EDGE,"E7.4.8")])],"isStart":false});
            var Q10;
            Q10=makeQuery(id+"F1.opExtrude","CAP_EDGE",EDGE,{"disambiguationData":[OSD([sQuery(id+"F0.wireOp",EDGE,"E7.4.8")])],"isStart":true});
            var Q11;
            Q11=makeQuery(id+"F1.opExtrude","CAP_EDGE",EDGE,{"disambiguationData":[OSD([sQuery(id+"F0.wireOp",EDGE,"E7.4.12")])],"isStart":true});
            var Q12;
            Q12=makeQuery(id+"F1.opExtrude","CAP_EDGE",EDGE,{"disambiguationData":[OSD([sQuery(id+"F0.wireOp",EDGE,"E7.1.8")])],"isStart":true});
            var Q13;
            Q13=makeQuery(id+"F1.opExtrude","CAP_EDGE",EDGE,{"disambiguationData":[OSD([sQuery(id+"F0.wireOp",EDGE,"E7.1.12")])],"isStart":true});
            var Q14;
            Q14=makeQuery(id+"F1.opExtrude","CAP_EDGE",EDGE,{"disambiguationData":[OSD([sQuery(id+"F0.wireOp",EDGE,"E7.1.12")])],"isStart":false});
            var Q15;
            Q15=makeQuery(id+"F1.opExtrude","CAP_EDGE",EDGE,{"disambiguationData":[OSD([sQuery(id+"F0.wireOp",EDGE,"E7.4.12")])],"isStart":false});
            var Q16;
            Q16=makeQuery(id+"F1.opExtrude","CAP_EDGE",EDGE,{"disambiguationData":[OSD([sQuery(id+"F0.wireOp",EDGE,"E7.1.8")])],"isStart":false});
            var Q17;
            Q17=makeQuery(id+"F1.opExtrude","CAP_EDGE",EDGE,{"disambiguationData":[OSD([sQuery(id+"F0.wireOp",EDGE,"E7.2.8")])],"isStart":false});
            var Q18;
            Q18=makeQuery(id+"F1.opExtrude","CAP_EDGE",EDGE,{"disambiguationData":[OSD([sQuery(id+"F0.wireOp",EDGE,"E5.1")])],"isStart":false});
            var Q19;
            Q19=makeQuery(id+"F1.opExtrude","CAP_EDGE",EDGE,{"disambiguationData":[OSD([sQuery(id+"F0.wireOp",EDGE,"E5.0")])],"isStart":false});
            fillet(context, id + "F5", {"entities" : qUnion([Q0, Q1, Q2, Q3, Q4, Q5, Q6, Q7, Q8, Q9, Q10, Q11, Q12, Q13, Q14, Q15, Q16, Q17, Q18, Q19]), "radius" : 1.4 * mm, "tangentPropagation" : true, "allowEdgeOverflow" : false});
        }
        {
            var Q0;
            Q0=makeQuery(id+"F1.opExtrude","CAP_FACE",FACE,{"disambiguationData":[OSD([sQuery(id+"F0.wireOp",EDGE,"E0"),sQuery(id+"F0.wireOp",EDGE,"E1"),sQuery(id+"F0.wireOp",EDGE,"E2.0"),sQuery(id+"F0.wireOp",EDGE,"E2.1"),sQuery(id+"F0.wireOp",EDGE,"E2.2"),sQuery(id+"F0.wireOp",EDGE,"E2.3"),sQuery(id+"F0.wireOp",EDGE,"E2.4"),sQuery(id+"F0.wireOp",EDGE,"E2.5"),sQuery(id+"F0.wireOp",EDGE,"E3"),sQuery(id+"F0.wireOp",EDGE,"E5.0"),sQuery(id+"F0.wireOp",EDGE,"E5.1"),sQuery(id+"F0.wireOp",EDGE,"E5.2"),sQuery(id+"F0.wireOp",EDGE,"E5.3"),sQuery(id+"F0.wireOp",EDGE,"E5.5"),sQuery(id+"F0.wireOp",EDGE,"E6"),sQuery(id+"F0.wireOp",EDGE,"E7.1.0"),sQuery(id+"F0.wireOp",EDGE,"E7.1.2"),sQuery(id+"F0.wireOp",EDGE,"E7.1.3"),sQuery(id+"F0.wireOp",EDGE,"E7.1.4"),sQuery(id+"F0.wireOp",EDGE,"E7.1.5"),sQuery(id+"F0.wireOp",EDGE,"E7.1.6"),sQuery(id+"F0.wireOp",EDGE,"E7.1.7"),sQuery(id+"F0.wireOp",EDGE,"E7.1.8"),sQuery(id+"F0.wireOp",EDGE,"E7.1.9"),sQuery(id+"F0.wireOp",EDGE,"E7.1.11"),sQuery(id+"F0.wireOp",EDGE,"E7.1.12"),sQuery(id+"F0.wireOp",EDGE,"E7.2.0"),sQuery(id+"F0.wireOp",EDGE,"E7.2.2"),sQuery(id+"F0.wireOp",EDGE,"E7.2.3"),sQuery(id+"F0.wireOp",EDGE,"E7.2.4"),sQuery(id+"F0.wireOp",EDGE,"E7.2.5"),sQuery(id+"F0.wireOp",EDGE,"E7.2.6"),sQuery(id+"F0.wireOp",EDGE,"E7.2.7"),sQuery(id+"F0.wireOp",EDGE,"E7.2.8"),sQuery(id+"F0.wireOp",EDGE,"E7.2.9"),sQuery(id+"F0.wireOp",EDGE,"E7.2.11"),sQuery(id+"F0.wireOp",EDGE,"E7.2.12"),sQuery(id+"F0.wireOp",EDGE,"E7.3.0"),sQuery(id+"F0.wireOp",EDGE,"E7.3.2"),sQuery(id+"F0.wireOp",EDGE,"E7.3.3"),sQuery(id+"F0.wireOp",EDGE,"E7.3.4"),sQuery(id+"F0.wireOp",EDGE,"E7.3.5"),sQuery(id+"F0.wireOp",EDGE,"E7.3.6"),sQuery(id+"F0.wireOp",EDGE,"E7.3.7"),sQuery(id+"F0.wireOp",EDGE,"E7.3.8"),sQuery(id+"F0.wireOp",EDGE,"E7.3.9"),sQuery(id+"F0.wireOp",EDGE,"E7.3.11"),sQuery(id+"F0.wireOp",EDGE,"E7.3.12"),sQuery(id+"F0.wireOp",EDGE,"E7.4.0"),sQuery(id+"F0.wireOp",EDGE,"E7.4.2"),sQuery(id+"F0.wireOp",EDGE,"E7.4.3"),sQuery(id+"F0.wireOp",EDGE,"E7.4.4"),sQuery(id+"F0.wireOp",EDGE,"E7.4.5"),sQuery(id+"F0.wireOp",EDGE,"E7.4.6"),sQuery(id+"F0.wireOp",EDGE,"E7.4.7"),sQuery(id+"F0.wireOp",EDGE,"E7.4.8"),sQuery(id+"F0.wireOp",EDGE,"E7.4.9"),sQuery(id+"F0.wireOp",EDGE,"E7.4.11"),sQuery(id+"F0.wireOp",EDGE,"E7.4.12")])],"isStart":false});
            var sketch = newSketch(context, id + "F6", { "sketchPlane" : qUnion([Q0])});
            skText(sketch, "E8", { "text": "A", "fontName": "RobotoSlab-Bold.ttf"});
            skPoint(sketch, "E9.center", {"position": v(0, 0) * mm});
            skCircle(sketch, "E10", {"center": v(0, 0) * mm, "radius": 16.09 * mm, "construction": true});
            skText(sketch, "E11", { "text": "R", "fontName": "RobotoSlab-Bold.ttf"});
            skText(sketch, "E12", { "text": "S", "fontName": "RobotoSlab-Bold.ttf"});
            skText(sketch, "E13", { "text": "E", "fontName": "RobotoSlab-Bold.ttf"});
            skText(sketch, "E14", { "text": "N", "fontName": "RobotoSlab-Bold.ttf"});
            skText(sketch, "E15", { "text": "E", "fontName": "RobotoSlab-Bold.ttf"});
            skText(sketch, "E16", { "text": "B", "fontName": "RobotoSlab-Bold.ttf"});
            skText(sketch, "E17", { "text": "E", "fontName": "RobotoSlab-Bold.ttf"});
            skText(sketch, "E18", { "text": "N", "fontName": "RobotoSlab-Bold.ttf"});
            skText(sketch, "E19", { "text": "O", "fontName": "RobotoSlab-Bold.ttf"});
            skText(sketch, "E20", { "text": "I", "fontName": "RobotoSlab-Bold.ttf"});
            skText(sketch, "E21", { "text": "T", "fontName": "RobotoSlab-Bold.ttf"});
            const initialGuessF6  = {"E8": [-0.0022, 0.01609, 1, 0, 0.0042], "E11": [0.0046, 0.01556, 0.91355, -0.40674, 0.0042], "E12": [0.0107, 0.01215, 0.66913, -0.74314, 0.0042], "E13": [0.01471, 0.00678, 0.30902, -0.95106, 0.0042], "E14": [0.01625, 0.00068, -0.10453, -0.99452, 0.0042], "E15": [0.01488, -0.0064, -0.5, -0.86603, 0.0042], "E16": [0.0018, -0.01535, -1, 0, 0.0042], "E17": [-0.00502, -0.01537, -0.91355, 0.40674, 0.0042], "E18": [-0.01052, -0.01236, -0.66913, 0.74314, 0.0042], "E19": [-0.01473, -0.00671, -0.30902, 0.95106, 0.00402], "E20": [-0.0161, 0.0008, 0.10453, 0.99452, 0.0042], "E21": [-0.01486, 0.00644, 0.5, 0.86603, 0.0042]};
            skSetInitialGuess(sketch, initialGuessF6);
            skSolve(sketch);
        }
        {
            var Q0;
            Q0 = qSketchRegion(id + "F6", true);
            extrude(context, id + "F7", {"entities" : qUnion([Q0]), "operationType" : NewBodyOperationType.ADD, "depth" : 0.8 * mm, "offsetDistance" : 25 * mm});
        }
        {
            var Q0;
            Q0=makeQuery(id+"F1.opExtrude","CAP_EDGE",EDGE,{"disambiguationData":[OSD([sQuery(id+"F0.wireOp",EDGE,"E7.1.2")])],"isStart":false});
            var Q1;
            Q1=makeQuery(id+"F1.opExtrude","CAP_EDGE",EDGE,{"disambiguationData":[OSD([sQuery(id+"F0.wireOp",EDGE,"E7.1.3")])],"isStart":false});
            var Q2;
            Q2=makeQuery(id+"F1.opExtrude","CAP_EDGE",EDGE,{"disambiguationData":[OSD([sQuery(id+"F0.wireOp",EDGE,"E7.1.7")])],"isStart":false});
            var Q3;
            Q3=makeQuery(id+"F1.opExtrude","CAP_EDGE",EDGE,{"disambiguationData":[OSD([sQuery(id+"F0.wireOp",EDGE,"E7.1.6")])],"isStart":false});
            var Q4;
            Q4=makeQuery(id+"F1.opExtrude","CAP_EDGE",EDGE,{"disambiguationData":[OSD([sQuery(id+"F0.wireOp",EDGE,"E7.1.5")])],"isStart":false});
            var Q5;
            Q5=makeQuery(id+"F1.opExtrude","CAP_EDGE",EDGE,{"disambiguationData":[OSD([sQuery(id+"F0.wireOp",EDGE,"E7.1.4")])],"isStart":false});
            var Q6;
            Q6=makeQuery(id+"F1.opExtrude","CAP_EDGE",EDGE,{"disambiguationData":[OSD([sQuery(id+"F0.wireOp",EDGE,"E2.0")])],"isStart":false});
            var Q7;
            Q7=makeQuery(id+"F1.opExtrude","CAP_EDGE",EDGE,{"disambiguationData":[OSD([sQuery(id+"F0.wireOp",EDGE,"E2.4")])],"isStart":false});
            var Q8;
            Q8=makeQuery(id+"F1.opExtrude","CAP_EDGE",EDGE,{"disambiguationData":[OSD([sQuery(id+"F0.wireOp",EDGE,"E2.3")])],"isStart":false});
            var Q9;
            Q9=makeQuery(id+"F1.opExtrude","CAP_EDGE",EDGE,{"disambiguationData":[OSD([sQuery(id+"F0.wireOp",EDGE,"E2.5")])],"isStart":false});
            var Q10;
            Q10=makeQuery(id+"F1.opExtrude","CAP_EDGE",EDGE,{"disambiguationData":[OSD([sQuery(id+"F0.wireOp",EDGE,"E2.1")])],"isStart":false});
            var Q11;
            Q11=makeQuery(id+"F1.opExtrude","CAP_EDGE",EDGE,{"disambiguationData":[OSD([sQuery(id+"F0.wireOp",EDGE,"E7.4.4")])],"isStart":false});
            var Q12;
            Q12=makeQuery(id+"F1.opExtrude","CAP_EDGE",EDGE,{"disambiguationData":[OSD([sQuery(id+"F0.wireOp",EDGE,"E7.4.5")])],"isStart":false});
            var Q13;
            Q13=makeQuery(id+"F1.opExtrude","CAP_EDGE",EDGE,{"disambiguationData":[OSD([sQuery(id+"F0.wireOp",EDGE,"E7.4.6")])],"isStart":false});
            var Q14;
            Q14=makeQuery(id+"F1.opExtrude","CAP_EDGE",EDGE,{"disambiguationData":[OSD([sQuery(id+"F0.wireOp",EDGE,"E7.4.3")])],"isStart":false});
            var Q15;
            Q15=makeQuery(id+"F1.opExtrude","CAP_EDGE",EDGE,{"disambiguationData":[OSD([sQuery(id+"F0.wireOp",EDGE,"E7.4.2")])],"isStart":false});
            var Q16;
            Q16=makeQuery(id+"F1.opExtrude","CAP_EDGE",EDGE,{"disambiguationData":[OSD([sQuery(id+"F0.wireOp",EDGE,"E7.4.7")])],"isStart":false});
            var Q17;
            Q17=makeQuery(id+"F1.opExtrude","CAP_EDGE",EDGE,{"disambiguationData":[OSD([sQuery(id+"F0.wireOp",EDGE,"E2.2")])],"isStart":false});
            var Q18;
            Q18=makeQuery(id+"F1.opExtrude","CAP_EDGE",EDGE,{"disambiguationData":[OSD([sQuery(id+"F0.wireOp",EDGE,"E7.2.3")])],"isStart":false});
            var Q19;
            Q19=makeQuery(id+"F1.opExtrude","CAP_EDGE",EDGE,{"disambiguationData":[OSD([sQuery(id+"F0.wireOp",EDGE,"E7.2.7")])],"isStart":false});
            var Q20;
            Q20=makeQuery(id+"F1.opExtrude","CAP_EDGE",EDGE,{"disambiguationData":[OSD([sQuery(id+"F0.wireOp",EDGE,"E7.2.6")])],"isStart":false});
            var Q21;
            Q21=makeQuery(id+"F1.opExtrude","CAP_EDGE",EDGE,{"disambiguationData":[OSD([sQuery(id+"F0.wireOp",EDGE,"E7.2.5")])],"isStart":false});
            var Q22;
            Q22=makeQuery(id+"F1.opExtrude","CAP_EDGE",EDGE,{"disambiguationData":[OSD([sQuery(id+"F0.wireOp",EDGE,"E7.2.4")])],"isStart":false});
            var Q23;
            Q23=makeQuery(id+"F1.opExtrude","CAP_EDGE",EDGE,{"disambiguationData":[OSD([sQuery(id+"F0.wireOp",EDGE,"E7.2.2")])],"isStart":false});
            var Q24;
            Q24=makeQuery(id+"F1.opExtrude","CAP_EDGE",EDGE,{"disambiguationData":[OSD([sQuery(id+"F0.wireOp",EDGE,"E7.3.6")])],"isStart":false});
            var Q25;
            Q25=makeQuery(id+"F1.opExtrude","CAP_EDGE",EDGE,{"disambiguationData":[OSD([sQuery(id+"F0.wireOp",EDGE,"E7.3.2")])],"isStart":false});
            var Q26;
            Q26=makeQuery(id+"F1.opExtrude","CAP_EDGE",EDGE,{"disambiguationData":[OSD([sQuery(id+"F0.wireOp",EDGE,"E7.3.4")])],"isStart":false});
            var Q27;
            Q27=makeQuery(id+"F1.opExtrude","CAP_EDGE",EDGE,{"disambiguationData":[OSD([sQuery(id+"F0.wireOp",EDGE,"E7.3.5")])],"isStart":false});
            var Q28;
            Q28=makeQuery(id+"F1.opExtrude","CAP_EDGE",EDGE,{"disambiguationData":[OSD([sQuery(id+"F0.wireOp",EDGE,"E7.3.3")])],"isStart":false});
            var Q29;
            Q29=makeQuery(id+"F1.opExtrude","CAP_EDGE",EDGE,{"disambiguationData":[OSD([sQuery(id+"F0.wireOp",EDGE,"E7.3.7")])],"isStart":false});
            var Q30;
            Q30=makeQuery(id+"F1.opExtrude","CAP_EDGE",EDGE,{"disambiguationData":[OSD([sQuery(id+"F0.wireOp",EDGE,"E7.3.6")])],"isStart":true});
            var Q31;
            Q31=makeQuery(id+"F1.opExtrude","CAP_EDGE",EDGE,{"disambiguationData":[OSD([sQuery(id+"F0.wireOp",EDGE,"E7.3.7")])],"isStart":true});
            var Q32;
            Q32=makeQuery(id+"F1.opExtrude","CAP_EDGE",EDGE,{"disambiguationData":[OSD([sQuery(id+"F0.wireOp",EDGE,"E7.3.5")])],"isStart":true});
            var Q33;
            Q33=makeQuery(id+"F1.opExtrude","CAP_EDGE",EDGE,{"disambiguationData":[OSD([sQuery(id+"F0.wireOp",EDGE,"E7.3.4")])],"isStart":true});
            var Q34;
            Q34=makeQuery(id+"F1.opExtrude","CAP_EDGE",EDGE,{"disambiguationData":[OSD([sQuery(id+"F0.wireOp",EDGE,"E7.3.2")])],"isStart":true});
            var Q35;
            Q35=makeQuery(id+"F1.opExtrude","CAP_EDGE",EDGE,{"disambiguationData":[OSD([sQuery(id+"F0.wireOp",EDGE,"E7.3.3")])],"isStart":true});
            var Q36;
            Q36=makeQuery(id+"F1.opExtrude","CAP_EDGE",EDGE,{"disambiguationData":[OSD([sQuery(id+"F0.wireOp",EDGE,"E7.2.4")])],"isStart":true});
            var Q37;
            Q37=makeQuery(id+"F1.opExtrude","CAP_EDGE",EDGE,{"disambiguationData":[OSD([sQuery(id+"F0.wireOp",EDGE,"E7.2.5")])],"isStart":true});
            var Q38;
            Q38=makeQuery(id+"F1.opExtrude","CAP_EDGE",EDGE,{"disambiguationData":[OSD([sQuery(id+"F0.wireOp",EDGE,"E7.2.6")])],"isStart":true});
            var Q39;
            Q39=makeQuery(id+"F1.opExtrude","CAP_EDGE",EDGE,{"disambiguationData":[OSD([sQuery(id+"F0.wireOp",EDGE,"E7.2.7")])],"isStart":true});
            var Q40;
            Q40=makeQuery(id+"F1.opExtrude","CAP_EDGE",EDGE,{"disambiguationData":[OSD([sQuery(id+"F0.wireOp",EDGE,"E7.2.3")])],"isStart":true});
            var Q41;
            Q41=makeQuery(id+"F1.opExtrude","CAP_EDGE",EDGE,{"disambiguationData":[OSD([sQuery(id+"F0.wireOp",EDGE,"E7.1.5")])],"isStart":true});
            var Q42;
            Q42=makeQuery(id+"F1.opExtrude","CAP_EDGE",EDGE,{"disambiguationData":[OSD([sQuery(id+"F0.wireOp",EDGE,"E7.1.6")])],"isStart":true});
            var Q43;
            Q43=makeQuery(id+"F1.opExtrude","CAP_EDGE",EDGE,{"disambiguationData":[OSD([sQuery(id+"F0.wireOp",EDGE,"E7.4.7")])],"isStart":true});
            var Q44;
            Q44=makeQuery(id+"F1.opExtrude","CAP_EDGE",EDGE,{"disambiguationData":[OSD([sQuery(id+"F0.wireOp",EDGE,"E7.4.3")])],"isStart":true});
            var Q45;
            Q45=makeQuery(id+"F1.opExtrude","CAP_EDGE",EDGE,{"disambiguationData":[OSD([sQuery(id+"F0.wireOp",EDGE,"E7.4.6")])],"isStart":true});
            var Q46;
            Q46=makeQuery(id+"F1.opExtrude","CAP_EDGE",EDGE,{"disambiguationData":[OSD([sQuery(id+"F0.wireOp",EDGE,"E7.4.5")])],"isStart":true});
            var Q47;
            Q47=makeQuery(id+"F1.opExtrude","CAP_EDGE",EDGE,{"disambiguationData":[OSD([sQuery(id+"F0.wireOp",EDGE,"E7.1.2")])],"isStart":true});
            var Q48;
            Q48=makeQuery(id+"F1.opExtrude","CAP_EDGE",EDGE,{"disambiguationData":[OSD([sQuery(id+"F0.wireOp",EDGE,"E7.1.3")])],"isStart":true});
            var Q49;
            Q49=makeQuery(id+"F1.opExtrude","CAP_EDGE",EDGE,{"disambiguationData":[OSD([sQuery(id+"F0.wireOp",EDGE,"E7.1.7")])],"isStart":true});
            var Q50;
            Q50=makeQuery(id+"F1.opExtrude","CAP_EDGE",EDGE,{"disambiguationData":[OSD([sQuery(id+"F0.wireOp",EDGE,"E2.5")])],"isStart":true});
            var Q51;
            Q51=makeQuery(id+"F1.opExtrude","CAP_EDGE",EDGE,{"disambiguationData":[OSD([sQuery(id+"F0.wireOp",EDGE,"E2.4")])],"isStart":true});
            var Q52;
            Q52=makeQuery(id+"F1.opExtrude","CAP_EDGE",EDGE,{"disambiguationData":[OSD([sQuery(id+"F0.wireOp",EDGE,"E2.0")])],"isStart":true});
            var Q53;
            Q53=makeQuery(id+"F1.opExtrude","CAP_EDGE",EDGE,{"disambiguationData":[OSD([sQuery(id+"F0.wireOp",EDGE,"E2.1")])],"isStart":true});
            var Q54;
            Q54=makeQuery(id+"F1.opExtrude","CAP_EDGE",EDGE,{"disambiguationData":[OSD([sQuery(id+"F0.wireOp",EDGE,"E2.2")])],"isStart":true});
            var Q55;
            Q55=makeQuery(id+"F1.opExtrude","CAP_EDGE",EDGE,{"disambiguationData":[OSD([sQuery(id+"F0.wireOp",EDGE,"E2.3")])],"isStart":true});
            var Q56;
            Q56=makeQuery(id+"F1.opExtrude","CAP_EDGE",EDGE,{"disambiguationData":[OSD([sQuery(id+"F0.wireOp",EDGE,"E7.1.4")])],"isStart":true});
            var Q57;
            Q57=makeQuery(id+"F1.opExtrude","CAP_EDGE",EDGE,{"disambiguationData":[OSD([sQuery(id+"F0.wireOp",EDGE,"E7.4.4")])],"isStart":true});
            var Q58;
            Q58=makeQuery(id+"F1.opExtrude","CAP_EDGE",EDGE,{"disambiguationData":[OSD([sQuery(id+"F0.wireOp",EDGE,"E7.4.2")])],"isStart":true});
            var Q59;
            Q59=makeQuery(id+"F1.opExtrude","CAP_EDGE",EDGE,{"disambiguationData":[OSD([sQuery(id+"F0.wireOp",EDGE,"E7.2.2")])],"isStart":true});
            chamfer(context, id + "F8", {"entities" : qUnion([Q0, Q1, Q2, Q3, Q4, Q5, Q6, Q7, Q8, Q9, Q10, Q11, Q12, Q13, Q14, Q15, Q16, Q17, Q18, Q19, Q20, Q21, Q22, Q23, Q24, Q25, Q26, Q27, Q28, Q29, Q30, Q31, Q32, Q33, Q34, Q35, Q36, Q37, Q38, Q39, Q40, Q41, Q42, Q43, Q44, Q45, Q46, Q47, Q48, Q49, Q50, Q51, Q52, Q53, Q54, Q55, Q56, Q57, Q58, Q59]), "width" : 0.3 * mm, "tangentPropagation" : true});
        }
        {
            var Q0;
            Q0=makeQuery(id+"F1.opExtrude","SWEPT_EDGE",EDGE,{"disambiguationData":[OSD([sQuery(id+"F0.wireOp",EDGE,"E5.0"),sQuery(id+"F0.wireOp",EDGE,"E5.3")])]});
            var Q1;
            Q1=makeQuery(id+"F1.opExtrude","SWEPT_EDGE",EDGE,{"disambiguationData":[OSD([sQuery(id+"F0.wireOp",EDGE,"E5.1"),sQuery(id+"F0.wireOp",EDGE,"E5.3")])]});
            var Q2;
            Q2=makeQuery(id+"F1.opExtrude","SWEPT_EDGE",EDGE,{"disambiguationData":[OSD([sQuery(id+"F0.wireOp",EDGE,"E7.1.0"),sQuery(id+"F0.wireOp",EDGE,"E7.1.8")])]});
            var Q3;
            Q3=makeQuery(id+"F1.opExtrude","SWEPT_EDGE",EDGE,{"disambiguationData":[OSD([sQuery(id+"F0.wireOp",EDGE,"E7.4.0"),sQuery(id+"F0.wireOp",EDGE,"E7.4.8")])]});
            var Q4;
            Q4=makeQuery(id+"F1.opExtrude","SWEPT_EDGE",EDGE,{"disambiguationData":[OSD([sQuery(id+"F0.wireOp",EDGE,"E7.4.0"),sQuery(id+"F0.wireOp",EDGE,"E7.4.12")])]});
            var Q5;
            Q5=makeQuery(id+"F1.opExtrude","SWEPT_EDGE",EDGE,{"disambiguationData":[OSD([sQuery(id+"F0.wireOp",EDGE,"E7.3.0"),sQuery(id+"F0.wireOp",EDGE,"E7.3.12")])]});
            var Q6;
            Q6=makeQuery(id+"F1.opExtrude","SWEPT_EDGE",EDGE,{"disambiguationData":[OSD([sQuery(id+"F0.wireOp",EDGE,"E7.3.0"),sQuery(id+"F0.wireOp",EDGE,"E7.3.8")])]});
            var Q7;
            Q7=makeQuery(id+"F1.opExtrude","SWEPT_EDGE",EDGE,{"disambiguationData":[OSD([sQuery(id+"F0.wireOp",EDGE,"E7.2.0"),sQuery(id+"F0.wireOp",EDGE,"E7.2.12")])]});
            var Q8;
            Q8=makeQuery(id+"F1.opExtrude","SWEPT_EDGE",EDGE,{"disambiguationData":[OSD([sQuery(id+"F0.wireOp",EDGE,"E7.2.0"),sQuery(id+"F0.wireOp",EDGE,"E7.2.8")])]});
            var Q9;
            Q9=makeQuery(id+"F1.opExtrude","SWEPT_EDGE",EDGE,{"disambiguationData":[OSD([sQuery(id+"F0.wireOp",EDGE,"E7.1.0"),sQuery(id+"F0.wireOp",EDGE,"E7.1.12")])]});
            fillet(context, id + "F9", {"entities" : qUnion([Q0, Q1, Q2, Q3, Q4, Q5, Q6, Q7, Q8, Q9]), "radius" : 1 * mm, "tangentPropagation" : true, "allowEdgeOverflow" : false});
        }
    });
